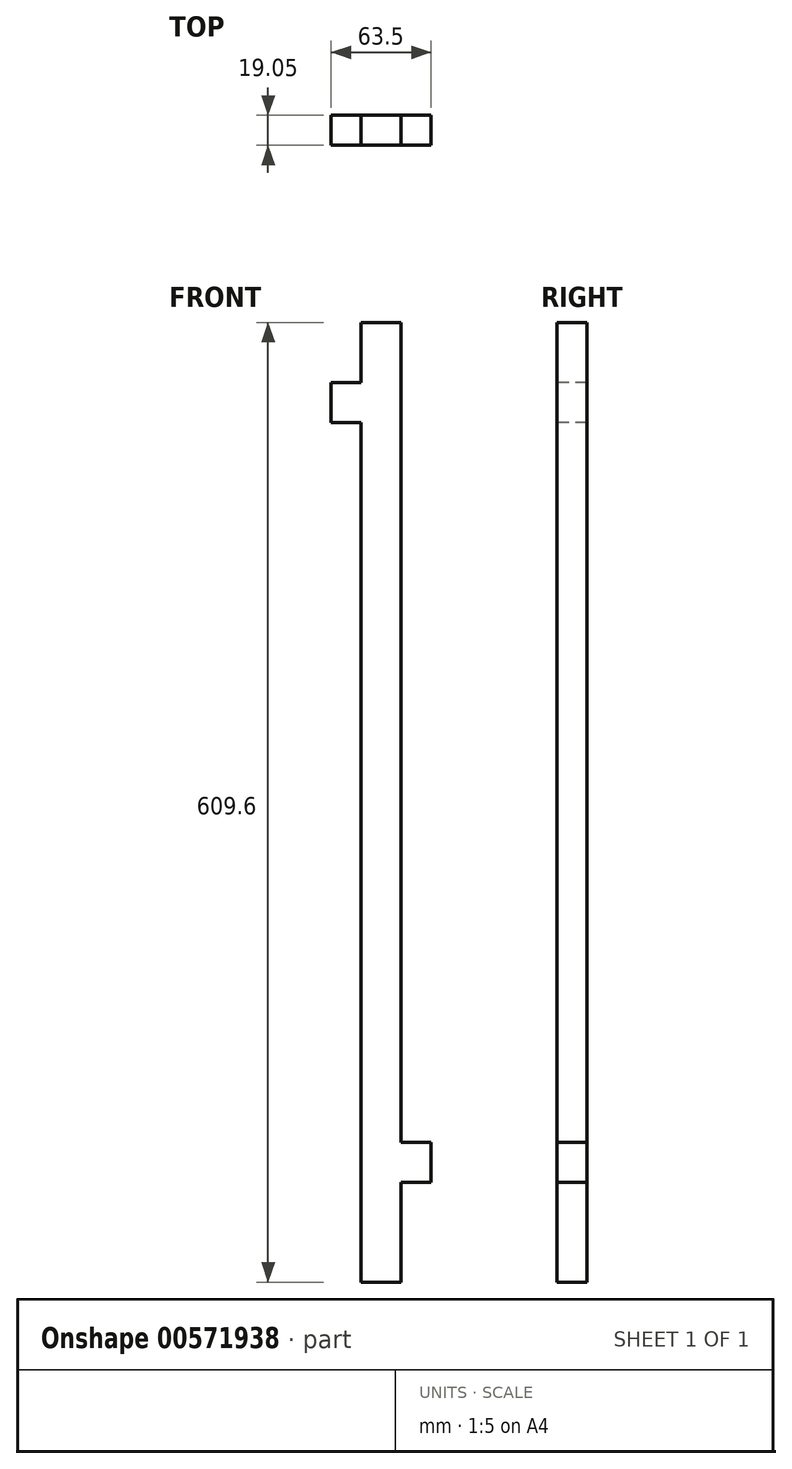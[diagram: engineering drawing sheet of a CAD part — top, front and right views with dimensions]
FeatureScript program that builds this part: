
annotation { "Feature Type Name" : "Feature", "Feature Type Description" : "" }
export const myFeature = defineFeature(function(context is Context, id is Id, definition is map)
    precondition{}
    {
        {
            var Q0;
            Q0=qCreatedBy(makeId("Front.planeOp"),FACE);
            var sketch = newSketch(context, id + "F0", { "sketchPlane" : qUnion([Q0])});
            skLineSegment(sketch, "E0.bottom", {"start": v(0, 0) * mm, "end": v(-25.4, 0) * mm});
            skLineSegment(sketch, "E0.top", {"start": v(0, -609.6) * mm, "end": v(-25.4, -609.6) * mm});
            skLineSegment(sketch, "E0.left", {"start": v(0, 0) * mm, "end": v(0, -609.6) * mm});
            skLineSegment(sketch, "E0.right", {"start": v(-25.4, 0) * mm, "end": v(-25.4, -609.6) * mm});
            skSolve(sketch);
        }
        {
            var Q0;
            Q0=makeQuery(id+"F0.imprint","IMPRINT",FACE,{"disambiguationData":[TD([[makeQuery(id+"F0.imprint","IMPRINT",EDGE,{"derivedFrom":sQuery(id+"F0.wireOp",EDGE,"E0.bottom")}),1.0]])]});
            extrude(context, id + "F1", {"entities" : qUnion([Q0]), "depth" : 19.05 * mm, "offsetDistance" : 25.4 * mm});
        }
        {
            var Q0;
            Q0=makeQuery(id+"F1.opExtrude","SWEPT_FACE",FACE,{"disambiguationData":[OSD([sQuery(id+"F0.wireOp",EDGE,"E0.right")])]});
            var sketch = newSketch(context, id + "F2", { "sketchPlane" : qUnion([Q0])});
            skLineSegment(sketch, "E1.bottom", {"start": v(0, -38.1) * mm, "end": v(19.05, -38.1) * mm});
            skLineSegment(sketch, "E1.top", {"start": v(0, -63.5) * mm, "end": v(19.05, -63.5) * mm});
            skLineSegment(sketch, "E1.left", {"start": v(0, -38.1) * mm, "end": v(0, -63.5) * mm});
            skLineSegment(sketch, "E1.right", {"start": v(19.05, -38.1) * mm, "end": v(19.05, -63.5) * mm});
            skSolve(sketch);
        }
        {
            var Q0;
            Q0=makeQuery(id+"F2.imprint","IMPRINT",FACE,{"disambiguationData":[TD([[makeQuery(id+"F2.imprint","IMPRINT",EDGE,{"derivedFrom":sQuery(id+"F2.wireOp",EDGE,"E1.bottom")}),-1.0]])]});
            extrude(context, id + "F3", {"entities" : qUnion([Q0]), "operationType" : NewBodyOperationType.ADD, "depth" : 19.05 * mm, "offsetDistance" : 25.4 * mm});
        }
        {
            var Q0;
            Q0=makeQuery(id+"F1.opExtrude","SWEPT_FACE",FACE,{"disambiguationData":[OSD([sQuery(id+"F0.wireOp",EDGE,"E0.left")])]});
            var sketch = newSketch(context, id + "F4", { "sketchPlane" : qUnion([Q0])});
            skLineSegment(sketch, "E2.bottom", {"start": v(-19.05, -520.7) * mm, "end": v(0, -520.7) * mm});
            skLineSegment(sketch, "E2.top", {"start": v(-19.05, -546.1) * mm, "end": v(0, -546.1) * mm});
            skLineSegment(sketch, "E2.left", {"start": v(-19.05, -520.7) * mm, "end": v(-19.05, -546.1) * mm});
            skLineSegment(sketch, "E2.right", {"start": v(0, -520.7) * mm, "end": v(0, -546.1) * mm});
            skSolve(sketch);
        }
        {
            var Q0;
            Q0 = qSketchRegion(id + "F4", true);
            extrude(context, id + "F5", {"entities" : qUnion([Q0]), "operationType" : NewBodyOperationType.ADD, "depth" : 19.05 * mm, "offsetDistance" : 25.4 * mm});
        }
    });
